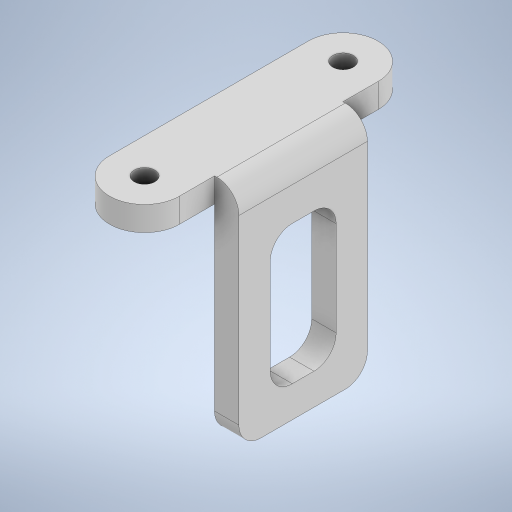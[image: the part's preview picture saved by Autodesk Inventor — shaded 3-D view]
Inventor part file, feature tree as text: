
AUTODESK INVENTOR PART (.ipt)
format: ipt  version: 2023 (Build 270158000, 158)  size: 288,768 bytes
history: native  units: in
note: dims shown in document units (in); Inventor stores cm internally (conversion verified against a paired STEP export)
features: extrude x3, sketch x3, fillet x1
ambient origin geometry x8: Origin, YZ Plane, XZ Plane, XY Plane, X Axis, Y Axis, Z Axis, Center Point
bodies: Solid1 (feature_tree)
feature tree (7):
  extrude  "Extrusion1"  Depth=0.116in
  sketch  "Sketch2"  dims[d3=0.395in d4=0.395in]
  extrude  "Extrusion4"  Depth=0.395in
  extrude  "Extrusion5"  Depth=0.125in
  fillet  "Fillet3"  Radius=0.198in
  sketch  "Sketch1"  dims[d0=0.116in d2=0.116in]
  sketch  "Sketch4"  dims[d5=0.1378in d6=0.0in d7=0.198in d8=0.198in d9=1.138in d10=0.25in d14=0.25in d17=0.125in d23=0.25in d25=0.125in d26=0.1378in d27=0.0in d29=0.1378in d30=0.0in d31=0.125in]
